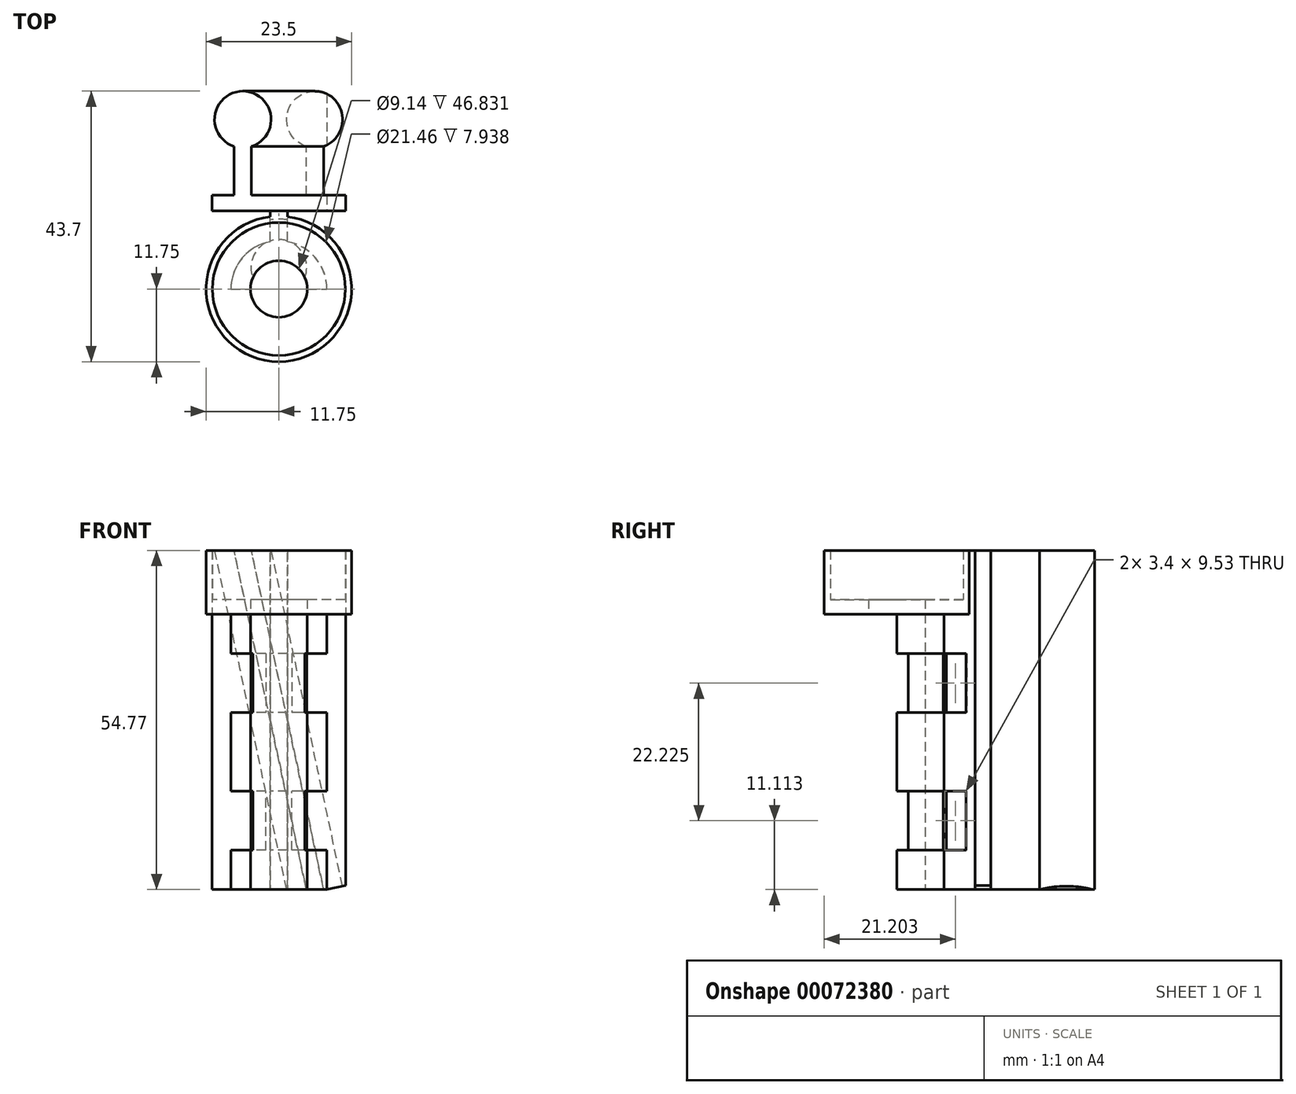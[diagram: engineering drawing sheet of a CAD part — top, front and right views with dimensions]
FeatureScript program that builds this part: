
annotation { "Feature Type Name" : "Feature", "Feature Type Description" : "" }
export const myFeature = defineFeature(function(context is Context, id is Id, definition is map)
    precondition{}
    {
        {
            var Q0;
            Q0=qCreatedBy(makeId("Top.planeOp"),FACE);
            var sketch = newSketch(context, id + "F0", { "sketchPlane" : qUnion([Q0])});
            skArc(sketch, "E0", {"start": v(4.57, 0) * mm, "mid": v(0, 4.57) * mm, "end": v(-4.57, 0) * mm});
            skArc(sketch, "E1", {"start": v(7.75, 0) * mm, "mid": v(0, 7.75) * mm, "end": v(-7.75, 0) * mm});
            skLineSegment(sketch, "E2", {"start": v(-7.75, 0) * mm, "end": v(-4.57, 0) * mm});
            skLineSegment(sketch, "E3", {"start": v(4.57, 0) * mm, "end": v(7.75, 0) * mm});
            skCircle(sketch, "E4", {"center": v(0, 23.73) * mm, "radius": 4.57 * mm});
            skLineSegment(sketch, "E5.rect.bottom", {"start": v(1.4, 7.62) * mm, "end": v(-1.4, 7.62) * mm, "construction": true});
            skLineSegment(sketch, "E5.rect.top", {"start": v(1.4, 19.38) * mm, "end": v(-1.4, 19.38) * mm, "construction": true});
            skLineSegment(sketch, "E5.rect.left", {"start": v(1.4, 7.62) * mm, "end": v(1.4, 19.38) * mm});
            skLineSegment(sketch, "E5.rect.right", {"start": v(-1.4, 7.62) * mm, "end": v(-1.4, 19.38) * mm});
            skPoint(sketch, "E5.rect.middle", {"position": v(0, 13.5) * mm});
            skSolve(sketch);
        }
        {
            var Q0;
            Q0=qSketchRegion(id+"F0",true);
            extrude(context, id + "F1", {"entities" : qUnion([Q0]), "depth" : 44.45 * mm});
        }
        {
            var Q0;
            Q0=makeQuery(id+"F1.opExtrude","SWEPT_FACE",FACE,{"disambiguationData":[OSD([sQuery(id+"F0.wireOp",EDGE,"E5.rect.left")])]});
            var sketch = newSketch(context, id + "F2", { "sketchPlane" : qUnion([Q0])});
            skLineSegment(sketch, "E6.bottom", {"start": v(7.62, 3.18) * mm, "end": v(10.8, 3.18) * mm});
            skLineSegment(sketch, "E6.top", {"start": v(7.62, 12.7) * mm, "end": v(10.8, 12.7) * mm});
            skLineSegment(sketch, "E6.left", {"start": v(7.62, 3.17) * mm, "end": v(7.62, 12.7) * mm});
            skLineSegment(sketch, "E6.right", {"start": v(10.8, 3.18) * mm, "end": v(10.8, 12.7) * mm});
            skLineSegment(sketch, "E7.bottom", {"start": v(7.62, 31.75) * mm, "end": v(10.8, 31.75) * mm});
            skLineSegment(sketch, "E7.top", {"start": v(7.62, 41.28) * mm, "end": v(10.8, 41.28) * mm});
            skLineSegment(sketch, "E7.left", {"start": v(7.62, 31.75) * mm, "end": v(7.62, 41.28) * mm});
            skLineSegment(sketch, "E7.right", {"start": v(10.8, 31.75) * mm, "end": v(10.8, 41.28) * mm});
            skLineSegment(sketch, "E8", {"start": v(10.8, 41.28) * mm, "end": v(10.8, 44.45) * mm, "construction": true});
            skLineSegment(sketch, "E9", {"start": v(10.8, 3.18) * mm, "end": v(10.8, 0) * mm, "construction": true});
            skLineSegment(sketch, "E10.rect.bottom", {"start": v(2.38, 41.28) * mm, "end": v(-2.38, 41.28) * mm});
            skLineSegment(sketch, "E10.rect.top", {"start": v(2.38, 31.75) * mm, "end": v(-2.38, 31.75) * mm});
            skLineSegment(sketch, "E10.rect.left", {"start": v(2.38, 41.28) * mm, "end": v(2.38, 31.75) * mm});
            skLineSegment(sketch, "E10.rect.right", {"start": v(-2.38, 41.28) * mm, "end": v(-2.38, 31.75) * mm});
            skPoint(sketch, "E10.rect.middle", {"position": v(0, 36.51) * mm});
            skLineSegment(sketch, "E11.rect.bottom", {"start": v(2.38, 3.17) * mm, "end": v(-2.38, 3.17) * mm});
            skLineSegment(sketch, "E11.rect.top", {"start": v(2.38, 12.7) * mm, "end": v(-2.38, 12.7) * mm});
            skLineSegment(sketch, "E11.rect.left", {"start": v(2.38, 3.18) * mm, "end": v(2.38, 12.7) * mm});
            skLineSegment(sketch, "E11.rect.right", {"start": v(-2.38, 3.18) * mm, "end": v(-2.38, 12.7) * mm});
            skPoint(sketch, "E11.rect.middle", {"position": v(0, 7.94) * mm});
            skSolve(sketch);
        }
        {
            var Q0;
            Q0=qCreatedBy(makeId("Top.planeOp"),FACE);
            var sketch = newSketch(context, id + "F3", { "sketchPlane" : qUnion([Q0])});
            skCircle(sketch, "E12", {"center": v(0, 1.78) * mm, "radius": 2.8 * mm, "construction": true});
            skLineSegment(sketch, "E13", {"start": v(-2.68, 4.57) * mm, "end": v(4.01, 4.57) * mm, "construction": true});
            skLineSegment(sketch, "E14", {"start": v(-3.3, -1.02) * mm, "end": v(3.4, -1.02) * mm, "construction": true});
            skCircle(sketch, "E15", {"center": v(0, 3.48) * mm, "radius": 4.5 * mm});
            skCircle(sketch, "E16", {"center": v(0, 3.48) * mm, "radius": 7.8 * mm});
            skLineSegment(sketch, "E17.bottom", {"start": v(-8.86, 1.25) * mm, "end": v(11.53, 1.25) * mm});
            skLineSegment(sketch, "E17.top", {"start": v(-8.86, -6.45) * mm, "end": v(11.53, -6.45) * mm});
            skLineSegment(sketch, "E17.left", {"start": v(-8.86, 1.25) * mm, "end": v(-8.86, -6.45) * mm});
            skLineSegment(sketch, "E17.right", {"start": v(11.53, 1.25) * mm, "end": v(11.53, -6.45) * mm});
            skSolve(sketch);
        }
        {
            var Q0;
            Q0=qCreatedBy(makeId("Top.planeOp"),FACE);
            var Q1;
            Q1=makeQuery(id+"F1.opExtrude","CAP_FACE",FACE,{"disambiguationData":[OSD([sQuery(id+"F0.wireOp",EDGE,"E0"),sQuery(id+"F0.wireOp",EDGE,"E1"),sQuery(id+"F0.wireOp",EDGE,"E2"),sQuery(id+"F0.wireOp",EDGE,"E3"),sQuery(id+"F0.wireOp",EDGE,"E4"),sQuery(id+"F0.wireOp",EDGE,"E5.rect.left"),sQuery(id+"F0.wireOp",EDGE,"E5.rect.right")])],"isStart":false});
            cPlane(context, id + "F4", {"entities" : qUnion([Q0, Q1]), "cplaneType" : CPlaneType.MID_PLANE, "offset" : 152.4 * mm, "width" : 152.4 * mm, "height" : 152.4 * mm});
        }
        {
            var Q0;
            Q0=qCreatedBy(id+"F4.planeOp",FACE);
            cPlane(context, id + "F5", {"entities" : qUnion([Q0]), "cplaneType" : CPlaneType.OFFSET, "offset" : 6.35 * mm, "width" : 152.4 * mm, "height" : 152.4 * mm});
        }
        {
            var Q0;
            Q0=qCreatedBy(id+"F5.planeOp",FACE);
            var sketch = newSketch(context, id + "F6", { "sketchPlane" : qUnion([Q0])});
            skCircle(sketch, "E18", {"center": v(0, 3.48) * mm, "radius": 4.5 * mm});
            skCircle(sketch, "E19", {"center": v(0, 3.48) * mm, "radius": 7.8 * mm});
            skLineSegment(sketch, "E20.bottom", {"start": v(-8.42, 1.76) * mm, "end": v(11.76, 1.76) * mm});
            skLineSegment(sketch, "E20.top", {"start": v(-8.42, -6.32) * mm, "end": v(11.76, -6.32) * mm});
            skLineSegment(sketch, "E20.left", {"start": v(-8.42, 1.76) * mm, "end": v(-8.42, -6.32) * mm});
            skLineSegment(sketch, "E20.right", {"start": v(11.76, 1.76) * mm, "end": v(11.76, -6.32) * mm});
            skSolve(sketch);
        }
        {
            var Q0;
            Q0=qCreatedBy(id+"F4.planeOp",FACE);
            cPlane(context, id + "F7", {"entities" : qUnion([Q0]), "cplaneType" : CPlaneType.OFFSET, "offset" : 6.35 * mm, "oppositeDirection" : true, "width" : 152.4 * mm, "height" : 152.4 * mm});
        }
        {
            var Q0;
            Q0=qCreatedBy(id+"F7.planeOp",FACE);
            var sketch = newSketch(context, id + "F8", { "sketchPlane" : qUnion([Q0])});
            skCircle(sketch, "E21", {"center": v(0, 3.48) * mm, "radius": 4.5 * mm});
            skCircle(sketch, "E22", {"center": v(0, 3.48) * mm, "radius": 7.8 * mm});
            skLineSegment(sketch, "E23.bottom", {"start": v(-8.58, 1.82) * mm, "end": v(8.4, 1.82) * mm});
            skLineSegment(sketch, "E23.top", {"start": v(-8.58, -6) * mm, "end": v(8.4, -6) * mm});
            skLineSegment(sketch, "E23.left", {"start": v(-8.58, 1.82) * mm, "end": v(-8.58, -6) * mm});
            skLineSegment(sketch, "E23.right", {"start": v(8.4, 1.82) * mm, "end": v(8.4, -6) * mm});
            skSolve(sketch);
        }
        {
            var Q0;
            Q0=makeQuery(id+"F6.imprint","IMPRINT",FACE,{"disambiguationData":[TD([[makeQuery(id+"F6.imprint","IMPRINT",EDGE,{"derivedFrom":sQuery(id+"F6.wireOp",EDGE,"E18")}),-1.0]])]});
            var Q1;
            Q1=makeQuery(id+"F6.imprint","IMPRINT",FACE,{"disambiguationData":[TD([[makeQuery(id+"F6.imprint","IMPRINT",EDGE,{"derivedFrom":sQuery(id+"F6.wireOp",EDGE,"E20.top")}),1.0]])]});
            extrude(context, id + "F9", {"entities" : qUnion([Q0, Q1]), "operationType" : NewBodyOperationType.REMOVE, "depth" : 9.52 * mm});
        }
        {
            var Q0;
            Q0=makeQuery(id+"F8.imprint","IMPRINT",FACE,{"disambiguationData":[TD([[makeQuery(id+"F8.imprint","IMPRINT",EDGE,{"derivedFrom":sQuery(id+"F8.wireOp",EDGE,"E21")}),-1.0]])]});
            var Q1;
            Q1=makeQuery(id+"F8.imprint","IMPRINT",FACE,{"disambiguationData":[TD([[makeQuery(id+"F8.imprint","IMPRINT",EDGE,{"derivedFrom":sQuery(id+"F8.wireOp",EDGE,"E23.top")}),1.0]])]});
            extrude(context, id + "F10", {"entities" : qUnion([Q0, Q1]), "operationType" : NewBodyOperationType.REMOVE, "oppositeDirection" : true, "depth" : 9.52 * mm});
        }
        {
            var Q0;
            Q0=makeQuery(id+"F1.opExtrude","CAP_FACE",FACE,{"disambiguationData":[OSD([sQuery(id+"F0.wireOp",EDGE,"E0"),sQuery(id+"F0.wireOp",EDGE,"E1"),sQuery(id+"F0.wireOp",EDGE,"E2"),sQuery(id+"F0.wireOp",EDGE,"E3"),sQuery(id+"F0.wireOp",EDGE,"E4"),sQuery(id+"F0.wireOp",EDGE,"E5.rect.left"),sQuery(id+"F0.wireOp",EDGE,"E5.rect.right")])],"isStart":false});
            var sketch = newSketch(context, id + "F11", { "sketchPlane" : qUnion([Q0])});
            skCircle(sketch, "E24", {"center": v(0, 0) * mm, "radius": 11.75 * mm});
            skCircle(sketch, "E25", {"center": v(0, 0) * mm, "radius": 4.57 * mm});
            skSolve(sketch);
        }
        {
            var Q0;
            {var subQ0=sQuery(id+"F0.wireOp",EDGE,"E2");var subQ9=makeQuery(id+"F1.opExtrude","CAP_EDGE",EDGE,{"disambiguationData":[OSD([subQ0])],"isStart":false});Q0=makeQuery(id+"F11.imprint","IMPRINT",FACE,{"disambiguationData":[TD([[makeQuery(id+"F11.imprint","IMPRINT",EDGE,{"derivedFrom":subQ9}),-1.0]])]});}
            var Q1;
            {var subQ0=sQuery(id+"F0.wireOp",EDGE,"E2");var subQ9=makeQuery(id+"F1.opExtrude","CAP_EDGE",EDGE,{"disambiguationData":[OSD([subQ0])],"isStart":false});Q1=makeQuery(id+"F11.imprint","IMPRINT",FACE,{"disambiguationData":[TD([[makeQuery(id+"F11.imprint","IMPRINT",EDGE,{"derivedFrom":subQ9}),1.0]])]});}
            extrude(context, id + "F12", {"entities" : qUnion([Q0, Q1]), "operationType" : NewBodyOperationType.ADD, "depth" : 2.38 * mm});
        }
        {
            var Q0;
            Q0=makeQuery(id+"F12.opExtrude","CAP_FACE",FACE,{"disambiguationData":[OSD([sQuery(id+"F11.wireOp",EDGE,"E24"),sQuery(id+"F11.wireOp",EDGE,"E25")])],"isStart":false});
            var sketch = newSketch(context, id + "F13", { "sketchPlane" : qUnion([Q0])});
            skCircle(sketch, "E26", {"center": v(0, 0) * mm, "radius": 11.75 * mm});
            skCircle(sketch, "E27", {"center": v(0, 0) * mm, "radius": 10.73 * mm});
            skSolve(sketch);
        }
        {
            var Q0;
            Q0=qSketchRegion(id+"F13",true);
            extrude(context, id + "F14", {"entities" : qUnion([Q0]), "operationType" : NewBodyOperationType.ADD, "depth" : 7.94 * mm});
        }
        {
            var Q0;
            Q0=makeQuery(id+"F1.opExtrude","CAP_FACE",FACE,{"disambiguationData":[OSD([sQuery(id+"F0.wireOp",EDGE,"E0"),sQuery(id+"F0.wireOp",EDGE,"E1"),sQuery(id+"F0.wireOp",EDGE,"E2"),sQuery(id+"F0.wireOp",EDGE,"E3"),sQuery(id+"F0.wireOp",EDGE,"E4"),sQuery(id+"F0.wireOp",EDGE,"E5.rect.left"),sQuery(id+"F0.wireOp",EDGE,"E5.rect.right")])],"isStart":false});
            var Q1;
            Q1=makeQuery(id+"F14.opExtrude","CAP_FACE",FACE,{"disambiguationData":[OSD([sQuery(id+"F13.wireOp",EDGE,"E26"),sQuery(id+"F13.wireOp",EDGE,"E27")])],"isStart":false});
            extrude(context, id + "F15", {"entities" : qUnion([Q0]), "operationType" : NewBodyOperationType.ADD, "endBound" : BoundingType.UP_TO_SURFACE, "endBoundEntityFace" : qUnion([Q1]), "depth" : 25.4 * mm});
        }
        {
            var Q0;
            Q0=qCreatedBy(makeId("Right.planeOp"),FACE);
            var sketch = newSketch(context, id + "F16", { "sketchPlane" : qUnion([Q0])});
            skLineSegment(sketch, "E28.bottom", {"start": v(12.6, 56.6) * mm, "end": v(39.56, 56.6) * mm});
            skLineSegment(sketch, "E28.top", {"start": v(12.6, -1.28) * mm, "end": v(39.56, -1.28) * mm});
            skLineSegment(sketch, "E28.left", {"start": v(12.6, 56.6) * mm, "end": v(12.6, -1.28) * mm});
            skLineSegment(sketch, "E28.right", {"start": v(39.56, 56.6) * mm, "end": v(39.56, -1.28) * mm});
            skSolve(sketch);
        }
        {
            var Q0;
            Q0 = qSketchRegion(id + "F16", true);
            extrude(context, id + "F17", {"entities" : qUnion([Q0]), "operationType" : NewBodyOperationType.REMOVE, "endBound" : BoundingType.SYMMETRIC, "oppositeDirection" : true, "depth" : 25.4 * mm});
        }
        {
            var Q0;
            Q0=makeQuery(id+"F17.boolean.opBoolean","COPY",FACE,{"derivedFrom":makeQuery(id+"F17.opExtrude","SWEPT_FACE",FACE,{"disambiguationData":[OSD([sQuery(id+"F16.wireOp",EDGE,"E28.left")])]})});
            cPlane(context, id + "F18", {"entities" : qUnion([Q0]), "cplaneType" : CPlaneType.OFFSET, "offset" : 0 * mm, "width" : 152.4 * mm, "height" : 152.4 * mm});
        }
        {
            var Q0;
            Q0=qCreatedBy(id+"F18.planeOp",FACE);
            var sketch = newSketch(context, id + "F19", { "sketchPlane" : qUnion([Q0])});
            skLineSegment(sketch, "E29.bottom", {"start": v(10.8, 54.77) * mm, "end": v(-10.8, 54.77) * mm});
            skLineSegment(sketch, "E29.top", {"start": v(10.8, 0) * mm, "end": v(-10.8, 0) * mm});
            skLineSegment(sketch, "E29.left", {"start": v(10.8, 54.77) * mm, "end": v(10.8, 0) * mm});
            skLineSegment(sketch, "E29.right", {"start": v(-10.8, 54.77) * mm, "end": v(-10.8, 0) * mm});
            skPoint(sketch, "E29.middle", {"position": v(0, 27.38) * mm});
            skSolve(sketch);
        }
        {
            var Q0;
            Q0 = qSketchRegion(id + "F19", true);
            extrude(context, id + "F20", {"entities" : qUnion([Q0]), "depth" : 2.54 * mm});
        }
        {
            var Q0;
            Q0=makeQuery(id+"F20.opExtrude","SWEPT_FACE",FACE,{"disambiguationData":[OSD([sQuery(id+"F19.wireOp",EDGE,"E29.bottom")])]});
            var Q1;
            Q1=makeQuery(id+"F20.opExtrude","SWEPT_FACE",FACE,{"disambiguationData":[OSD([sQuery(id+"F19.wireOp",EDGE,"E29.top")])]});
            cPlane(context, id + "F21", {"entities" : qUnion([Q0, Q1]), "cplaneType" : CPlaneType.MID_PLANE, "offset" : 152.4 * mm, "width" : 152.4 * mm, "height" : 152.4 * mm});
        }
        {
            var Q0;
            Q0=qCreatedBy(id+"F21.planeOp",FACE);
            var sketch = newSketch(context, id + "F22", { "sketchPlane" : qUnion([Q0])});
            skLineSegment(sketch, "E30.bottom", {"start": v(-1.4, 15.15) * mm, "end": v(1.4, 15.15) * mm});
            skLineSegment(sketch, "E30.top", {"start": v(-1.4, 23.02) * mm, "end": v(1.4, 23.02) * mm, "construction": true});
            skLineSegment(sketch, "E30.left", {"start": v(-1.4, 15.15) * mm, "end": v(-1.4, 23.02) * mm});
            skLineSegment(sketch, "E30.right", {"start": v(1.4, 15.15) * mm, "end": v(1.4, 23.02) * mm});
            skPoint(sketch, "E30.middle", {"position": v(0, 19.08) * mm});
            skCircle(sketch, "E31", {"center": v(0, 27.37) * mm, "radius": 4.57 * mm});
            skSolve(sketch);
        }
        {
            var Q0;
            Q0=makeQuery(id+"F20.opExtrude","CAP_FACE",FACE,{"disambiguationData":[OSD([sQuery(id+"F19.wireOp",EDGE,"E29.bottom"),sQuery(id+"F19.wireOp",EDGE,"E29.top"),sQuery(id+"F19.wireOp",EDGE,"E29.left"),sQuery(id+"F19.wireOp",EDGE,"E29.right")])],"isStart":false});
            var sketch = newSketch(context, id + "F23", { "sketchPlane" : qUnion([Q0])});
            skLineSegment(sketch, "E32", {"start": v(-5.82, 0) * mm, "end": v(0, 27.38) * mm});
            skLineSegment(sketch, "E33", {"start": v(0, 27.38) * mm, "end": v(5.82, 54.77) * mm});
            skLineSegment(sketch, "E34", {"start": v(0, 27.38) * mm, "end": v(0, 65.36) * mm, "construction": true});
            skSolve(sketch);
        }
        {
            var Q0;
            {var subQ0=sQuery(id+"F22.wireOp",EDGE,"E31");var subQ1=makeQuery(id+"F22.imprint","INTERSECT",VERTEX,{"derivedFrom":[sQuery(id+"F22.wireOp",EDGE,"E30.left"),subQ0]});Q0=makeQuery(id+"F22.imprint","IMPRINT",FACE,{"disambiguationData":[TD([[makeQuery(id+"F22.imprint","IMPRINT",EDGE,{"disambiguationData":[TD([[subQ1,-1.0]])],"derivedFrom":subQ0}),1.0]])]});}
            var Q1;
            Q1=makeQuery(id+"F22.imprint","IMPRINT",FACE,{"disambiguationData":[TD([[makeQuery(id+"F22.imprint","IMPRINT",EDGE,{"derivedFrom":sQuery(id+"F22.wireOp",EDGE,"E30.bottom")}),1.0]])]});
            var Q2;
            Q2=sQuery(id+"F23.wireOp",EDGE,"E33");
            sweep(context, id + "F24", {"operationType" : NewBodyOperationType.ADD, "profiles" : qUnion([Q0, Q1]), "path" : qUnion([Q2])});
        }
        {
            var Q0;
            Q0 = qSketchRegion(id + "F22", true);
            var Q1;
            Q1=sQuery(id+"F23.wireOp",EDGE,"E32");
            sweep(context, id + "F25", {"operationType" : NewBodyOperationType.ADD, "profiles" : qUnion([Q0]), "path" : qUnion([Q1])});
        }
        {
            var Q0;
            Q0=makeQuery(id+"F20.opExtrude","CAP_FACE",FACE,{"disambiguationData":[OSD([sQuery(id+"F19.wireOp",EDGE,"E29.bottom"),sQuery(id+"F19.wireOp",EDGE,"E29.top"),sQuery(id+"F19.wireOp",EDGE,"E29.left"),sQuery(id+"F19.wireOp",EDGE,"E29.right")])],"isStart":true});
            var sketch = newSketch(context, id + "F26", { "sketchPlane" : qUnion([Q0])});
            skLineSegment(sketch, "E35", {"start": v(3.53, -0.9) * mm, "end": v(20.61, 2.73) * mm});
            skLineSegment(sketch, "E36", {"start": v(20.61, 2.73) * mm, "end": v(24.61, -1.82) * mm});
            skLineSegment(sketch, "E37", {"start": v(24.61, -1.82) * mm, "end": v(7.86, -6.5) * mm});
            skLineSegment(sketch, "E38", {"start": v(7.86, -6.5) * mm, "end": v(3.53, -0.9) * mm});
            skSolve(sketch);
        }
        {
            var Q0;
            {var subQ0=sQuery(id+"F26.wireOp",EDGE,"E36");Q0=makeQuery(id+"F26.imprint","IMPRINT",FACE,{"disambiguationData":[TD([[makeQuery(id+"F26.imprint","IMPRINT",EDGE,{"derivedFrom":subQ0}),-1.0]])]});}
            var Q1;
            {var subQ0=sQuery(id+"F26.wireOp",EDGE,"E35");var subQ1=makeQuery(id+"F20.opExtrude","CAP_EDGE",EDGE,{"disambiguationData":[OSD([sQuery(id+"F19.wireOp",EDGE,"E29.top")])],"isStart":true});var subQ2=makeQuery(id+"F26.imprint","INTERSECT",VERTEX,{"derivedFrom":[subQ1,subQ0]});Q1=makeQuery(id+"F26.imprint","IMPRINT",FACE,{"disambiguationData":[TD([[makeQuery(id+"F26.imprint","IMPRINT",EDGE,{"disambiguationData":[TD([[subQ2,-1.0]])],"derivedFrom":subQ0}),-1.0]])]});}
            extrude(context, id + "F27", {"entities" : qUnion([Q0, Q1]), "operationType" : NewBodyOperationType.REMOVE, "oppositeDirection" : true, "depth" : 25.4 * mm});
        }
    });
